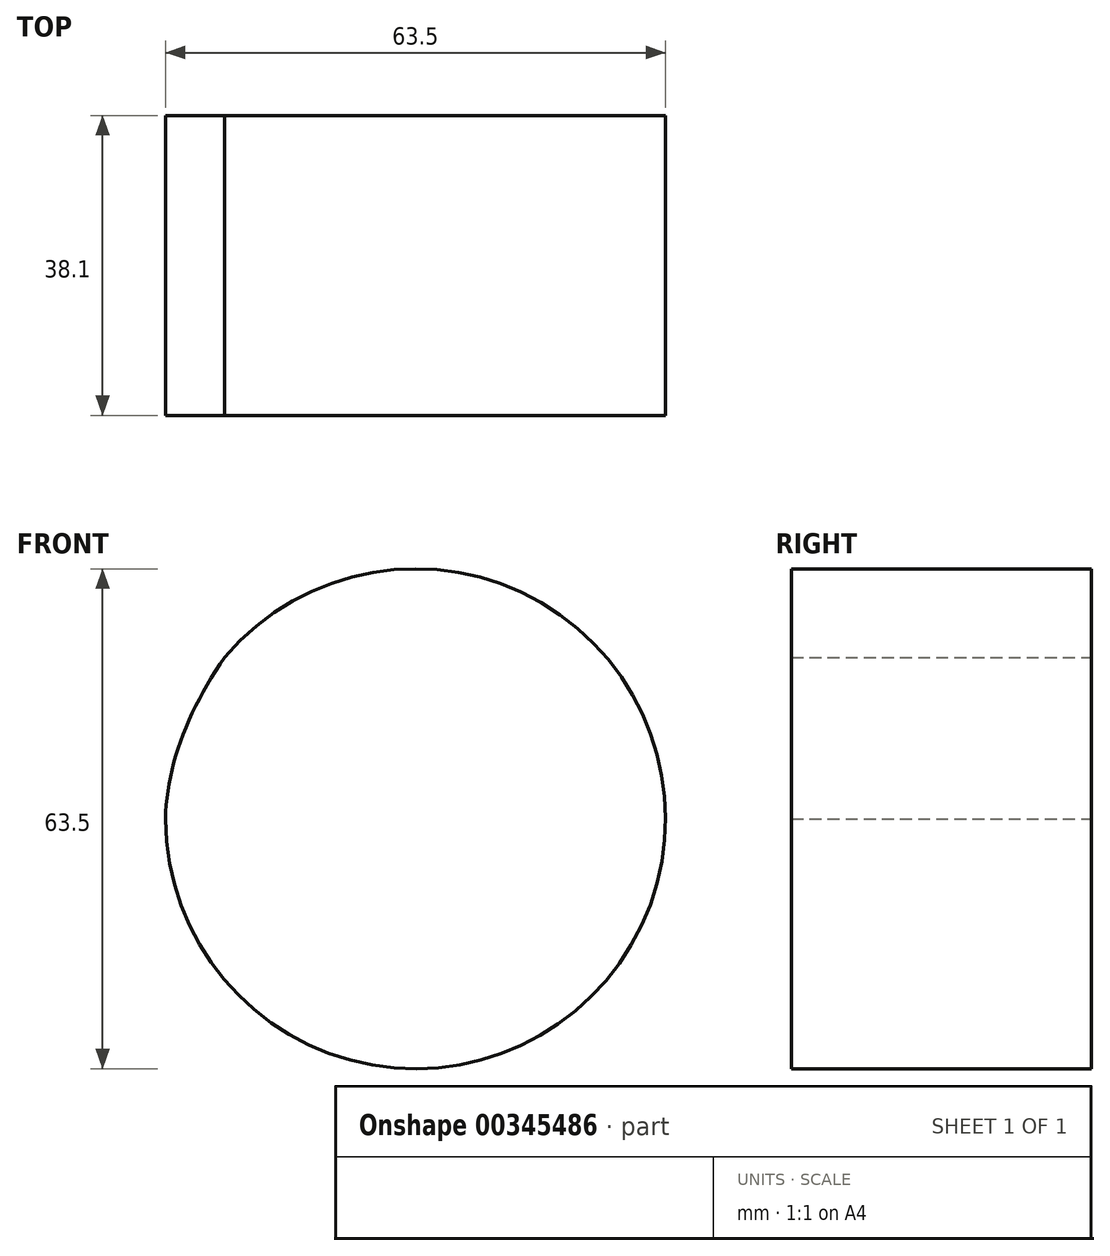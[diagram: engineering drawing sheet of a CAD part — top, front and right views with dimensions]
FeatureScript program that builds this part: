
annotation { "Feature Type Name" : "Feature", "Feature Type Description" : "" }
export const myFeature = defineFeature(function(context is Context, id is Id, definition is map)
    precondition{}
    {
        {
            var Q0;
            Q0=qCreatedBy(makeId("Front.planeOp"),FACE);
            var sketch = newSketch(context, id + "F0", { "sketchPlane" : qUnion([Q0])});
            skCircle(sketch, "E0", {"center": v(0, 0) * mm, "radius": 31.75 * mm});
            skCircle(sketch, "E1", {"center": v(51.14, 46.4) * mm, "radius": 31.75 * mm});
            skPoint(sketch, "E1.first.point", {"position": v(30.7, 70.7) * mm});
            skPoint(sketch, "E1.second.point", {"position": v(76.4, 27.17) * mm});
            skPoint(sketch, "E1.third.point", {"position": v(19.91, 52.13) * mm});
            skLineSegment(sketch, "E2", {"start": v(19.71, 41.9) * mm, "end": v(19.71, 49.92) * mm});
            skFitSpline(sketch, "E3", {"points": [v(-31.75, 0) * mm, v(19.71, 45.91) * mm], "startDerivative": vector(0.74, 62.23) * mm, "endDerivative": vector(73.27, -1.5) * mm});
            skSolve(sketch);
        }
        {
            var Q0;
            {var subQ0=sQuery(id+"F0.wireOp",EDGE,"E3");var subQ1=sQuery(id+"F0.wireOp",EDGE,"E0");var subQ2=makeQuery(id+"F0.imprint","INTERSECT",VERTEX,{"disambiguationData":[OD(0.0)],"derivedFrom":[subQ1,subQ0]});Q0=makeQuery(id+"F0.imprint","IMPRINT",FACE,{"disambiguationData":[TD([[makeQuery(id+"F0.imprint","IMPRINT",EDGE,{"disambiguationData":[TD([[subQ2,-1.0]])],"derivedFrom":subQ1}),1.0]])]});}
            extrude(context, id + "F1", {"entities" : qUnion([Q0]), "depth" : 38.1 * mm});
        }
    });
